# Revit family: Toilet Roll Dispenser_Metlam_Single_Surface Mounted
name_source: partatom
category: Specialty Equipment
revit_build: Autodesk Revit 2016 (Build: 20170117_1200(x64)
units: mm (PartAtom-declared; Revit-internal decimal feet)

## family parameters
Always vertical = Yes
Cut with Voids When Loaded = No
OmniClass Number = 23.40.20.21.21
OmniClass Title = Toilet Paper Dispensers
Part Type = Normal
Room Calculation Point = Yes
Round Connector Dimension = Use Diameter
Shared = No
Work Plane-Based = No

## types (1)
- 161w x 83d x 161h (ML260SM_S)
    Description = Single Toilet Roll Holder
    Manufacturer = Metlam
    Manufacturer_Overall Depth = 83 mm  [stored 0.27231 ft]
    Manufacturer_Overall Height = 161 mm  [stored 0.528215 ft]
    Manufacturer_Overall Width = 161 mm  [stored 0.528215 ft]
    Manufacturer_Spec Code = ML260SM_S
    Manufacturer_URL__Product Specific = https://www.metlam.com.au
    Material_ANZRS = z_Metlam_Metal_Stainless Steel_Satin
    Model = ML260SM_S
    Type Comments = Toilet Roll Dispensers
    URL = http://www.metlam.com.au

note: [stored X ft] marks values corroborated as IEEE doubles in the binary element streams (Revit-internal decimal feet)

## geometry (parser evidence)
native form markers: Sweep x3
no freeform markers — native parametric forms only
